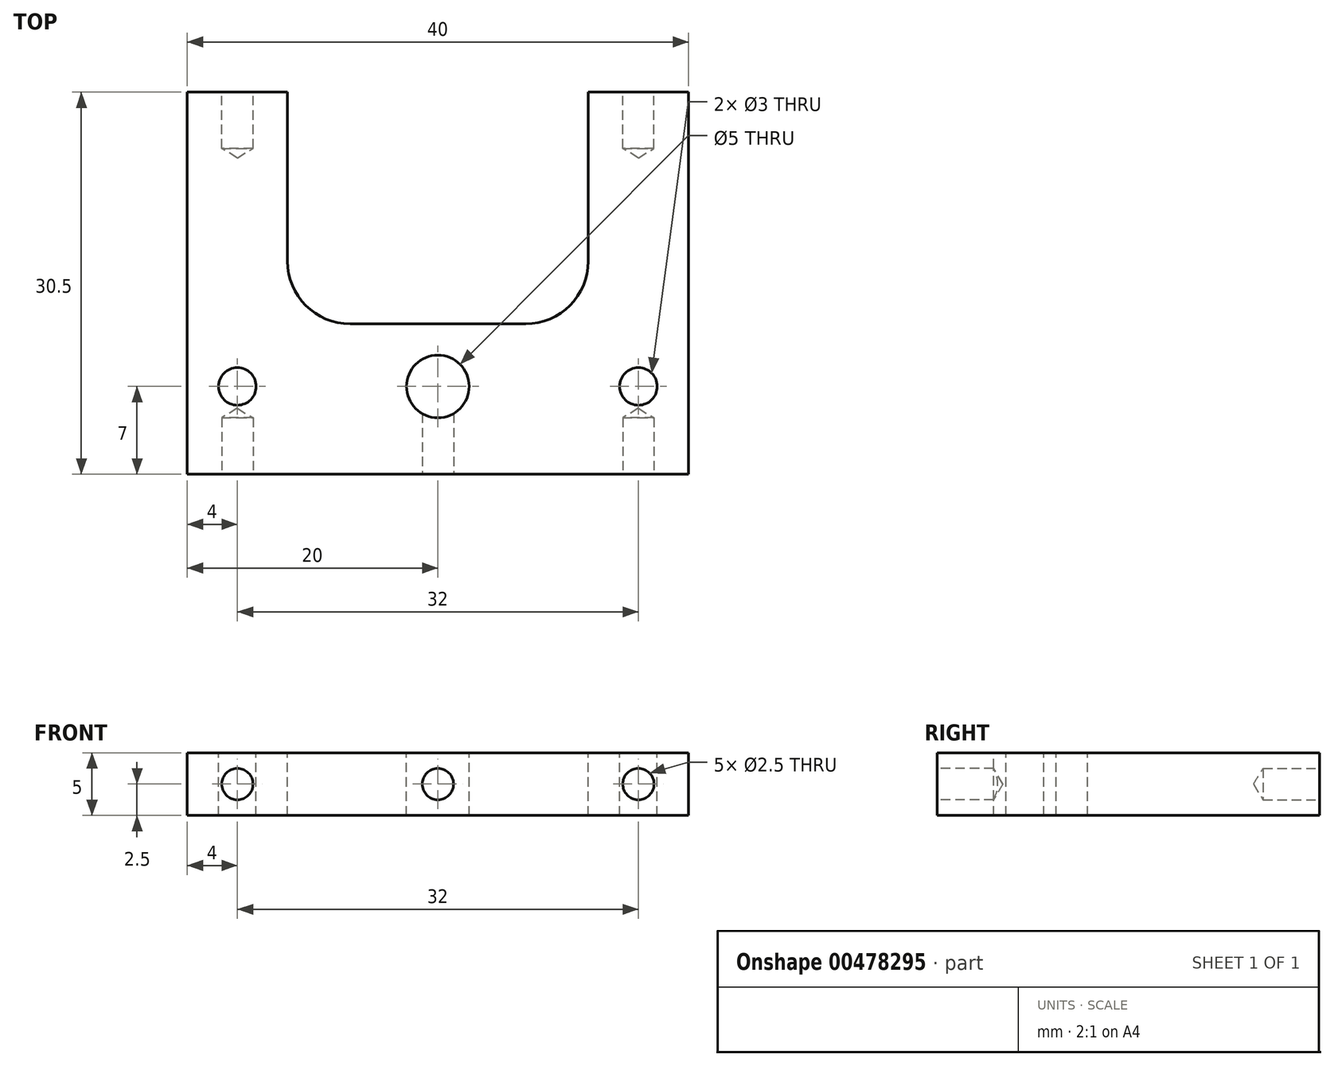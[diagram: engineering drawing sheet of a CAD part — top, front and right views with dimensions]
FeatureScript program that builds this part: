
annotation { "Feature Type Name" : "Feature", "Feature Type Description" : "" }
export const myFeature = defineFeature(function(context is Context, id is Id, definition is map)
    precondition{}
    {
        {
            var Q0;
            Q0=qCreatedBy(makeId("Top.planeOp"),FACE);
            var sketch = newSketch(context, id + "F0", { "sketchPlane" : qUnion([Q0])});
            skLineSegment(sketch, "E0.bottom", {"start": v(20, -15.25) * mm, "end": v(-20, -15.25) * mm});
            skLineSegment(sketch, "E0.top", {"start": v(20, 15.25) * mm, "end": v(-20, 15.25) * mm});
            skLineSegment(sketch, "E0.left", {"start": v(20, -15.25) * mm, "end": v(20, 15.25) * mm});
            skLineSegment(sketch, "E0.right", {"start": v(-20, -15.25) * mm, "end": v(-20, 15.25) * mm});
            skPoint(sketch, "E0.middle", {"position": v(0, 0) * mm});
            skPoint(sketch, "E1", {"position": v(-16, -8.25) * mm});
            skPoint(sketch, "E2", {"position": v(0, -8.25) * mm});
            skLineSegment(sketch, "E3", {"start": v(-12, 15.25) * mm, "end": v(-12, -3.25) * mm});
            skLineSegment(sketch, "E4", {"start": v(-12, -3.25) * mm, "end": v(12, -3.25) * mm});
            skLineSegment(sketch, "E5", {"start": v(12, -3.25) * mm, "end": v(12, 15.25) * mm});
            skPoint(sketch, "E6", {"position": v(0, -3.25) * mm});
            skPoint(sketch, "E7.MirrorP", {"position": v(16, -8.25) * mm});
            skSolve(sketch);
        }
        {
            var Q0;
            Q0=makeQuery(id+"F0.imprint","IMPRINT",FACE,{"disambiguationData":[TD([[makeQuery(id+"F0.imprint","IMPRINT",EDGE,{"derivedFrom":sQuery(id+"F0.wireOp",EDGE,"E0.bottom")}),-1.0]])]});
            extrude(context, id + "F1", {"entities" : qUnion([Q0]), "oppositeDirection" : true, "depth" : 5 * mm});
        }
        {
            var Q0;
            Q0=makeQuery(id+"F1.opExtrude","SWEPT_EDGE",EDGE,{"disambiguationData":[OSD([sQuery(id+"F0.wireOp",EDGE,"E3"),sQuery(id+"F0.wireOp",EDGE,"E4")])]});
            var Q1;
            Q1=makeQuery(id+"F1.opExtrude","SWEPT_EDGE",EDGE,{"disambiguationData":[OSD([sQuery(id+"F0.wireOp",EDGE,"E4"),sQuery(id+"F0.wireOp",EDGE,"E5")])]});
            fillet(context, id + "F2", {"entities" : qUnion([Q0, Q1]), "radius" : 5 * mm, "tangentPropagation" : true, "allowEdgeOverflow" : false});
        }
        {
            var Q0;
            Q0=sQuery(id+"F0.wireOp",VERTEX,"E1");
            var Q1;
            Q1=sQuery(id+"F0.wireOp",VERTEX,"E7.MirrorP");
            var Q2;
            Q2=makeQuery(id+"F1.opExtrude","SWEPT_BODY",BODY,{"disambiguationData":[OSD([sQuery(id+"F0.wireOp",EDGE,"E0.bottom"),sQuery(id+"F0.wireOp",EDGE,"E0.top"),sQuery(id+"F0.wireOp",EDGE,"E0.left"),sQuery(id+"F0.wireOp",EDGE,"E0.right"),sQuery(id+"F0.wireOp",EDGE,"E3"),sQuery(id+"F0.wireOp",EDGE,"E4"),sQuery(id+"F0.wireOp",EDGE,"E5")])]});
            hole(context, id + "F3", {"style" : HoleStyle.SIMPLE, "endStyle" : HoleEndStyle.THROUGH, "holeDiameter" : 3 * mm, "isTappedThrough" : true, "tappedDepth" : 12 * mm, "tapClearance" : 3, "startFromSketch" : true, "locations" : qUnion([Q0, Q1]), "scope" : qUnion([Q2])});
        }
        {
            var Q0;
            {var subQ0=sQuery(id+"F0.wireOp",EDGE,"E0.top");Q0=makeQuery(id+"F1.opExtrude","SWEPT_FACE",FACE,{"disambiguationData":[OSD([subQ0]),TDD([makeQuery(id+"F0.imprint","IMPRINT",EDGE,{"disambiguationData":[TD([[makeQuery(id+"F0.imprint","INTERSECT",VERTEX,{"derivedFrom":[subQ0,sQuery(id+"F0.wireOp",EDGE,"E0.left")]}),-1.0]])],"derivedFrom":subQ0})])]});}
            var sketch = newSketch(context, id + "F4", { "sketchPlane" : qUnion([Q0])});
            skPoint(sketch, "E8", {"position": v(-16, -2.5) * mm});
            skPoint(sketch, "E8.positionSnap0", {"position": v(-20, -2.5) * mm});
            skPoint(sketch, "E8.positionSnap1", {"position": v(-16, 0) * mm});
            skPoint(sketch, "E9.MirrorP", {"position": v(16, -2.5) * mm});
            skSolve(sketch);
        }
        {
            var Q0;
            Q0=makeQuery(id+"F1.opExtrude","SWEPT_FACE",FACE,{"disambiguationData":[OSD([sQuery(id+"F0.wireOp",EDGE,"E0.bottom")])]});
            var sketch = newSketch(context, id + "F5", { "sketchPlane" : qUnion([Q0])});
            skPoint(sketch, "E10", {"position": v(-16, -2.5) * mm});
            skPoint(sketch, "E11.MirrorP", {"position": v(16, -2.5) * mm});
            skPoint(sketch, "E12", {"position": v(0, -2.5) * mm});
            skSolve(sketch);
        }
        {
            var Q0;
            Q0=sQuery(id+"F4.wireOp",VERTEX,"E8");
            var Q1;
            Q1=sQuery(id+"F4.wireOp",VERTEX,"E9.MirrorP");
            var Q2;
            Q2=sQuery(id+"F5.wireOp",VERTEX,"E10");
            var Q3;
            Q3=sQuery(id+"F5.wireOp",VERTEX,"E11.MirrorP");
            var Q4;
            Q4=makeQuery(id+"F1.opExtrude","SWEPT_BODY",BODY,{"disambiguationData":[OSD([sQuery(id+"F0.wireOp",EDGE,"E0.bottom"),sQuery(id+"F0.wireOp",EDGE,"E0.top"),sQuery(id+"F0.wireOp",EDGE,"E0.left"),sQuery(id+"F0.wireOp",EDGE,"E0.right"),sQuery(id+"F0.wireOp",EDGE,"E3"),sQuery(id+"F0.wireOp",EDGE,"E4"),sQuery(id+"F0.wireOp",EDGE,"E5")])]});
            hole(context, id + "F6", {"style" : HoleStyle.SIMPLE, "endStyle" : HoleEndStyle.BLIND, "holeDiameter" : 2.5 * mm, "holeDepth" : 4.5 * mm, "isTappedThrough" : true, "tappedDepth" : 12 * mm, "tapClearance" : 3, "startFromSketch" : true, "locations" : qUnion([Q0, Q1, Q2, Q3]), "scope" : qUnion([Q4])});
        }
        {
            var Q0;
            Q0=sQuery(id+"F0.wireOp",VERTEX,"E2");
            var Q1;
            Q1=makeQuery(id+"F1.opExtrude","SWEPT_BODY",BODY,{"disambiguationData":[OSD([sQuery(id+"F0.wireOp",EDGE,"E0.bottom"),sQuery(id+"F0.wireOp",EDGE,"E0.top"),sQuery(id+"F0.wireOp",EDGE,"E0.left"),sQuery(id+"F0.wireOp",EDGE,"E0.right"),sQuery(id+"F0.wireOp",EDGE,"E3"),sQuery(id+"F0.wireOp",EDGE,"E4"),sQuery(id+"F0.wireOp",EDGE,"E5")])]});
            hole(context, id + "F7", {"style" : HoleStyle.SIMPLE, "endStyle" : HoleEndStyle.THROUGH, "holeDiameter" : 5 * mm, "isTappedThrough" : true, "tappedDepth" : 12 * mm, "tapClearance" : 3, "startFromSketch" : true, "locations" : qUnion([Q0]), "scope" : qUnion([Q1])});
        }
        {
            var Q0;
            Q0=sQuery(id+"F5.wireOp",VERTEX,"E12");
            var Q1;
            Q1=makeQuery(id+"F1.opExtrude","SWEPT_BODY",BODY,{"disambiguationData":[OSD([sQuery(id+"F0.wireOp",EDGE,"E0.bottom"),sQuery(id+"F0.wireOp",EDGE,"E0.top"),sQuery(id+"F0.wireOp",EDGE,"E0.left"),sQuery(id+"F0.wireOp",EDGE,"E0.right"),sQuery(id+"F0.wireOp",EDGE,"E3"),sQuery(id+"F0.wireOp",EDGE,"E4"),sQuery(id+"F0.wireOp",EDGE,"E5")])]});
            hole(context, id + "F8", {"style" : HoleStyle.SIMPLE, "endStyle" : HoleEndStyle.BLIND, "holeDiameter" : 2.5 * mm, "holeDepth" : 6 * mm, "isTappedThrough" : true, "tappedDepth" : 12 * mm, "tapClearance" : 3, "startFromSketch" : true, "locations" : qUnion([Q0]), "scope" : qUnion([Q1])});
        }
    });
